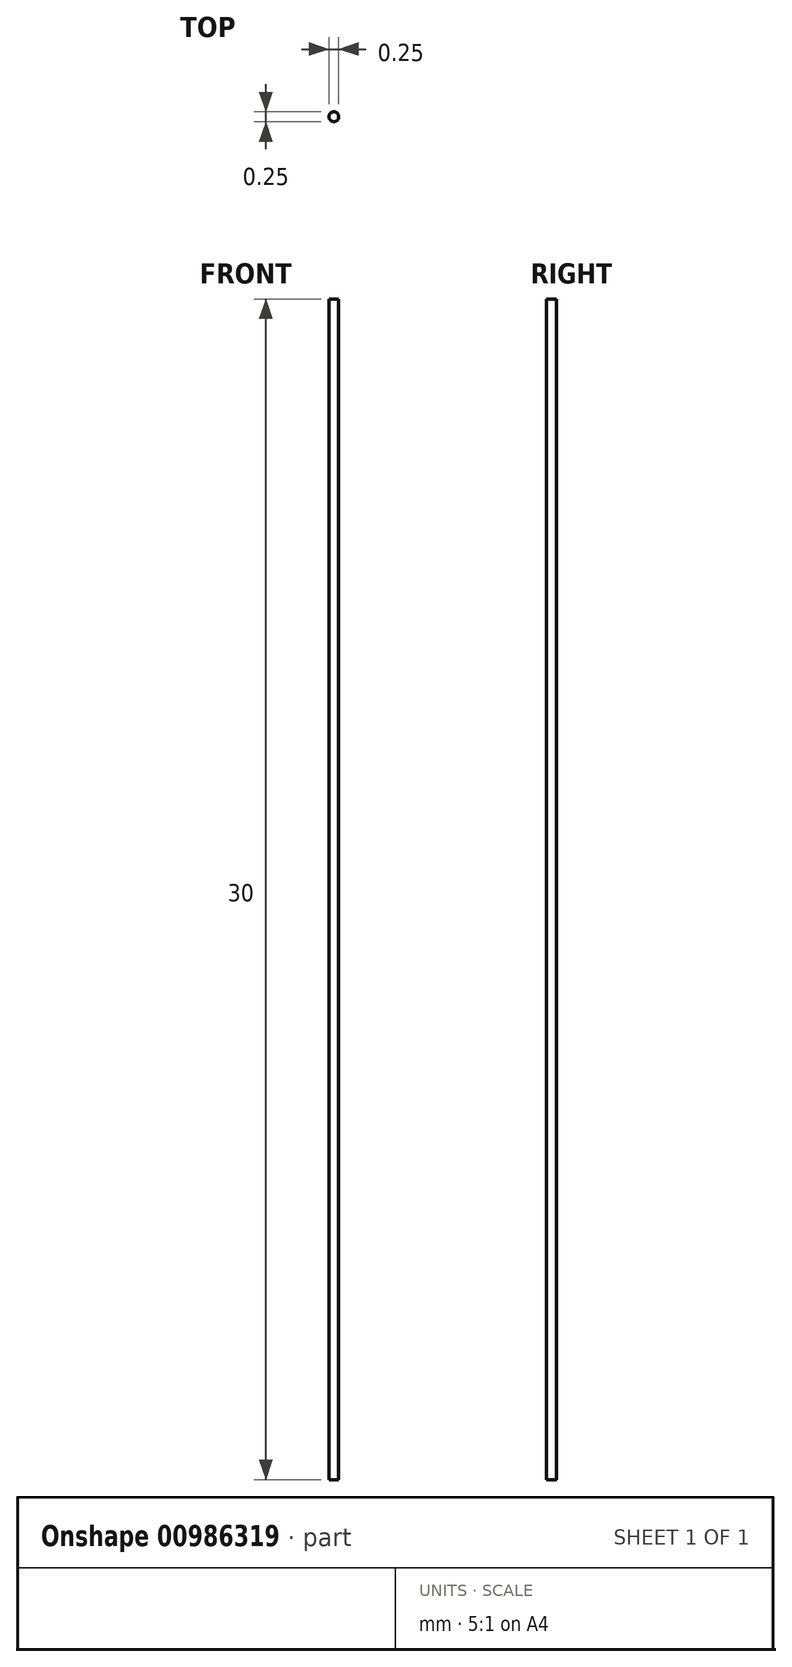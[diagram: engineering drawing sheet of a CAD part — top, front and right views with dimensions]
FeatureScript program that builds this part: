
annotation { "Feature Type Name" : "Feature", "Feature Type Description" : "" }
export const myFeature = defineFeature(function(context is Context, id is Id, definition is map)
    precondition{}
    {
        {
            var Q0;
            Q0=qCreatedBy(makeId("Top.planeOp"),FACE);
            var sketch = newSketch(context, id + "F0", { "sketchPlane" : qUnion([Q0])});
            skCircle(sketch, "E0", {"center": v(2.49, 0.2) * mm, "radius": 0.12 * mm});
            skSolve(sketch);
        }
        {
            var Q0;
            Q0 = qSketchRegion(id + "F0", true);
            extrude(context, id + "F1", {"entities" : qUnion([Q0]), "depth" : 30 * mm, "offsetDistance" : 25 * mm});
        }
    });
